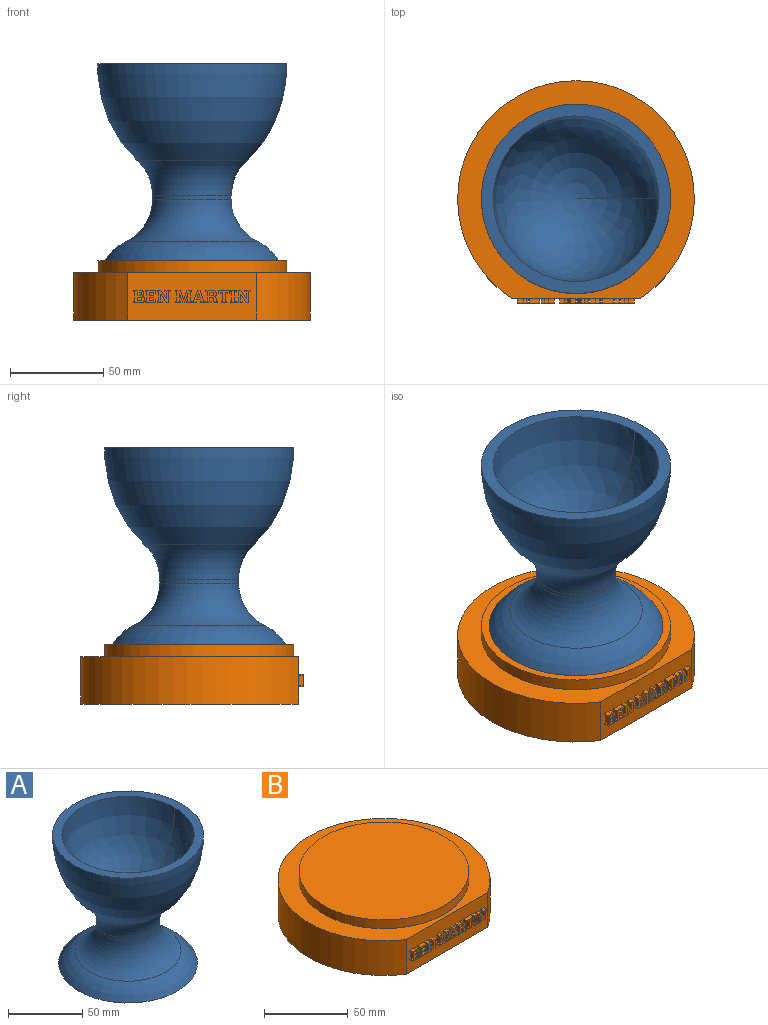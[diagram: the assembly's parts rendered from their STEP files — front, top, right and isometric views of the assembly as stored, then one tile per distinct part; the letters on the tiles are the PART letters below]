
ASSEMBLY  parts=2 mates=1
PART A: 10 faces, bbox 101.6x101.6x105.7 mm
  f0: plane 101.6x101.6mm, normal (0,0,1), area 1900.2mm2, adj f2,f7,f8,f9
  f1: cylinder r=21.22mm len=42.44mm, axis (0,0,-1), area 284.2mm2, adj f5,f6
  f2: revolved ~51.56x21.15mm, area 4.4mm2, adj f0,f6,f8
  f3: plane 93.24x93.24mm, normal (0,0,-1), area 6828.6mm2, adj f4
  f4: torus R=24.62mm, axis (0,0,1), area 3982.6mm2, adj f3,f5
  f5: torus R=46.62mm, axis (0,0,-1), area 4701.5mm2, adj f1,f4
  f6: torus R=46.62mm, axis (0,0,-1), area 3226.2mm2, adj f1,f2,f8
  f7: revolved ~57.15x44.45mm, area 4.1mm2, adj f0,f9
  f8: revolved ~101.6x101.6mm, area 15777.6mm2, adj f0,f2,f6
  f9: revolved ~88.9x88.9mm, area 14832.9mm2, adj f0,f7
PART B: 225 faces, bbox 127x119.4x31.8 mm
  f0: plane 68.91x25.4mm, normal (0,-1,0), area 1517.6mm2, adj f1,f2,f3,f18,f19,f20,f21,f22
  f1: plane 127x116.84mm, normal (0,0,-1), area 12192.9mm2, adj f0,f2
  f2: cylinder r=63.5mm len=127mm, axis (0,0,1), area 8284.1mm2, adj f0,f1,f3
  f3: plane 127x116.84mm, normal (0,0,1), area 4085.6mm2, adj f0,f2,f4
  f4: cylinder r=50.8mm len=101.6mm, axis (0,0,1), area 2026.8mm2, adj f3,f5
  f5: plane 101.6x101.6mm, normal (0,0,1), area 8107.3mm2, adj f4
  f6: plane 2.54x1mm, normal (0,0,1), area 2.5mm2, adj f7,f34,f35,f36
  f7: plane 2.54x1.84mm, normal (1,0,0), area 4.7mm2, adj f6,f8,f35,f36
  f8: plane 2.54x0.95mm, normal (0,0,-1), area 2.4mm2, adj f7,f9,f35,f36
  f9: extruded ~2.54x0.9mm, area 2.4mm2, adj f8,f10,f35,f36
  f10: extruded ~2.54x0.71mm, area 2mm2, adj f9,f11,f35,f36
  f11: extruded ~2.54x0.67mm, area 1.9mm2, adj f10,f34,f35,f36
  f12: plane 2.54x2mm, normal (1,0,0), area 5.1mm2, adj f13,f32,f35,f37
  f13: plane 2.54x1.39mm, normal (0,0,-1), area 3.5mm2, adj f12,f14,f35,f37
  f14: extruded ~2.54x0.78mm, area 2.2mm2, adj f13,f15,f35,f37
  f15: extruded ~2.54x0.78mm, area 2.1mm2, adj f14,f16,f35,f37
  f16: extruded ~2.54x0.71mm, area 2mm2, adj f15,f17,f35,f37
  f17: extruded ~2.54x0.84mm, area 2.3mm2, adj f16,f32,f35,f37
  f18: extruded ~2.54x1.91mm, area 5.1mm2, adj f0,f19,f33,f35
  f19: plane 3.09x2.54mm, normal (0,0,1), area 7.8mm2, adj f0,f18,f20,f35
  f20: plane 2.54x0.84mm, normal (-1,0,0), area 2.1mm2, adj f0,f19,f21,f35
  f21: plane 2.54x0.74mm, normal (-0.19,0,-0.98), area 1.9mm2, adj f0,f20,f22,f35
  f22: plane 4.98x2.54mm, normal (-1,0,0), area 12.7mm2, adj f0,f21,f23,f35
  f23: plane 2.54x0.74mm, normal (-0.19,0,0.98), area 1.9mm2, adj f0,f22,f24,f35
  f24: plane 2.54x0.84mm, normal (-1,0,0), area 2.1mm2, adj f0,f23,f25,f35
  f25: plane 3.42x2.54mm, normal (0,0,-1), area 8.7mm2, adj f0,f24,f26,f35
  f26: extruded ~2.54x1.86mm, area 5mm2, adj f0,f25,f27,f35
  f27: extruded ~2.54x1.51mm, area 4.3mm2, adj f0,f26,f28,f35
  f28: extruded ~2.54x1.02mm, area 2.7mm2, adj f0,f27,f29,f35
  f29: extruded ~2.54x0.94mm, area 2.9mm2, adj f0,f28,f30,f35
  f30: extruded ~2.54x0.74mm, area 2.4mm2, adj f0,f29,f31,f35
  f31: extruded ~2.54x0.86mm, area 2.3mm2, adj f0,f30,f33,f35
  f32: plane 2.54x1.28mm, normal (0,0,1), area 3.3mm2, adj f12,f17,f35,f37
  f33: extruded ~2.54x1.43mm, area 4.2mm2, adj f0,f18,f31,f35
  f34: extruded ~2.54x0.86mm, area 2.3mm2, adj f6,f11,f35,f36
  f35: plane 6.94x5.94mm, normal (0,-1,0), area 25.9mm2, adj f6,f7,f8,f9,f10,f11,f12,f13
  f36: plane 2.16x1.84mm, normal (0,-1,0), area 3.6mm2, adj f6,f7,f8,f9,f10,f11,f34
  f37: plane 2.42x2mm, normal (0,-1,0), area 4.5mm2, adj f12,f13,f14,f15,f16,f17,f32
  f38: plane 2.54x2.35mm, normal (0,0,-1), area 6mm2, adj f0,f39,f57,f58
  f39: plane 2.54x1.07mm, normal (1,0,0), area 2.7mm2, adj f0,f38,f40,f58
  f40: plane 2.54x2.35mm, normal (0,0,1), area 6mm2, adj f0,f39,f41,f58
  f41: plane 2.54x1.75mm, normal (1,0,0), area 4.4mm2, adj f0,f40,f42,f58
  f42: plane 2.54x2.22mm, normal (0,0,-1), area 5.6mm2, adj f0,f41,f43,f58
  f43: plane 2.54x0.83mm, normal (-1,0,-0.08), area 2.1mm2, adj f0,f42,f44,f58
  f44: plane 2.54x1.07mm, normal (0,0,-1), area 2.7mm2, adj f0,f43,f45,f58
  f45: plane 2.54x1.9mm, normal (1,0,0), area 4.8mm2, adj f0,f44,f46,f58
  f46: plane 5.49x2.54mm, normal (0,0,1), area 13.9mm2, adj f0,f45,f47,f58
  f47: plane 2.54x0.84mm, normal (-1,0,0), area 2.1mm2, adj f0,f46,f48,f58
  f48: plane 2.54x0.74mm, normal (-0.19,0,-0.98), area 1.9mm2, adj f0,f47,f49,f58
  f49: plane 4.98x2.54mm, normal (-1,0,0), area 12.7mm2, adj f0,f48,f50,f58
  f50: plane 2.54x0.74mm, normal (-0.19,0,0.98), area 1.9mm2, adj f0,f49,f51,f58
  f51: plane 2.54x0.84mm, normal (-1,0,0), area 2.1mm2, adj f0,f50,f52,f58
  f52: plane 5.49x2.54mm, normal (0,0,-1), area 14mm2, adj f0,f51,f53,f58
  f53: plane 2.54x1.9mm, normal (1,0,0), area 4.8mm2, adj f0,f52,f54,f58
  f54: plane 2.54x1.06mm, normal (0,0,1), area 2.7mm2, adj f0,f53,f55,f58
  f55: plane 2.54x0.83mm, normal (-1,0,0.07), area 2.1mm2, adj f0,f54,f56,f58
  f56: plane 2.54x2.24mm, normal (0,0,1), area 5.7mm2, adj f0,f55,f57,f58
  f57: plane 2.54x1.98mm, normal (1,0,0), area 5mm2, adj f0,f38,f56,f58
  f58: plane 6.94x5.49mm, normal (0,-1,0), area 22.6mm2, adj f38,f39,f40,f41,f42,f43,f44,f45
  f59: plane 2.54x0.84mm, normal (1,0,0), area 2.1mm2, adj f0,f60,f80,f81
  f60: plane 2.88x2.54mm, normal (0,0,1), area 7.3mm2, adj f0,f59,f61,f81
  f61: plane 2.54x0.84mm, normal (-1,0,0), area 2.1mm2, adj f0,f60,f62,f81
  f62: plane 2.54x0.74mm, normal (-0.19,0,-0.98), area 1.9mm2, adj f0,f61,f63,f81
  f63: plane 3.69x2.54mm, normal (-1,0,0), area 9.4mm2, adj f0,f62,f64,f81
  f64: plane 2.54x0.03mm, normal (-0.16,0,0.99), area 0.1mm2, adj f0,f63,f65,f81
  f65: plane 4.67x2.8mm, normal (0.86,0,0.51), area 13.8mm2, adj f0,f64,f66,f81
  f66: plane 2.54x2.13mm, normal (0,0,1), area 5.4mm2, adj f0,f65,f67,f81
  f67: plane 2.54x0.84mm, normal (-1,0,0), area 2.1mm2, adj f0,f66,f68,f81
  f68: plane 2.54x0.74mm, normal (-0.19,0,-0.98), area 1.9mm2, adj f0,f67,f69,f81
  f69: plane 4.98x2.54mm, normal (-1,0,0), area 12.7mm2, adj f0,f68,f70,f81
  f70: plane 2.54x0.74mm, normal (-0.19,0,0.98), area 1.9mm2, adj f0,f69,f71,f81
  f71: plane 2.54x0.84mm, normal (-1,0,0), area 2.1mm2, adj f0,f70,f72,f81
  f72: plane 2.88x2.54mm, normal (0,0,-1), area 7.3mm2, adj f0,f71,f73,f81
  f73: plane 2.54x0.84mm, normal (1,0,0), area 2.1mm2, adj f0,f72,f74,f81
  f74: plane 2.54x0.74mm, normal (0.19,0,0.98), area 1.9mm2, adj f0,f73,f75,f81
  f75: plane 3.69x2.54mm, normal (1,0,0), area 9.4mm2, adj f0,f74,f76,f81
  f76: plane 2.54x0.03mm, normal (0.21,0,-0.98), area 0.1mm2, adj f0,f75,f77,f81
  f77: plane 4.68x2.8mm, normal (-0.86,0,-0.51), area 13.8mm2, adj f0,f76,f78,f81
  f78: plane 2.54x1.39mm, normal (0,0,-1), area 3.5mm2, adj f0,f77,f79,f81
  f79: plane 5.96x2.54mm, normal (1,0,0), area 15.1mm2, adj f0,f78,f80,f81
  f80: plane 2.54x0.74mm, normal (0.19,0,-0.98), area 1.9mm2, adj f0,f59,f79,f81
  f81: plane 7.1x6.94mm, normal (0,-1,0), area 29mm2, adj f59,f60,f61,f62,f63,f64,f65,f66
  f82: plane 2.54x0.03mm, normal (-0.16,0,-0.99), area 0.1mm2, adj f0,f83,f111,f112
  f83: plane 3.07x2.54mm, normal (-1,0,0.04), area 7.8mm2, adj f0,f82,f84,f112
  f84: plane 2.54x1.09mm, normal (-1,0,0), area 2.8mm2, adj f0,f83,f85,f112
  f85: plane 2.54x0.74mm, normal (-0.19,0,0.98), area 1.9mm2, adj f0,f84,f86,f112
  f86: plane 2.54x0.84mm, normal (-1,0,0), area 2.1mm2, adj f0,f85,f87,f112
  f87: plane 2.88x2.54mm, normal (0,0,-1), area 7.3mm2, adj f0,f86,f88,f112
  f88: plane 2.54x0.84mm, normal (1,0,0), area 2.1mm2, adj f0,f87,f89,f112
  f89: plane 2.54x0.74mm, normal (0.19,0,0.98), area 1.9mm2, adj f0,f88,f90,f112
  f90: plane 4.98x2.54mm, normal (1,0,0), area 12.7mm2, adj f0,f89,f91,f112
  f91: plane 2.54x0.74mm, normal (0.19,0,-0.98), area 1.9mm2, adj f0,f90,f92,f112
  f92: plane 2.54x0.84mm, normal (1,0,0), area 2.1mm2, adj f0,f91,f93,f112
  f93: plane 2.57x2.54mm, normal (0,0,1), area 6.5mm2, adj f0,f92,f94,f112
  f94: plane 5.12x2.54mm, normal (-0.94,0,0.33), area 13.8mm2, adj f0,f93,f95,f112
  f95: plane 2.54x0.03mm, normal (0,0,1), area 0.1mm2, adj f0,f94,f96,f112
  f96: plane 5.12x2.54mm, normal (0.95,0,0.33), area 13.8mm2, adj f0,f95,f97,f112
  f97: plane 2.56x2.54mm, normal (0,0,1), area 6.5mm2, adj f0,f96,f98,f112
  f98: plane 2.54x0.84mm, normal (-1,0,0), area 2.1mm2, adj f0,f97,f99,f112
  f99: plane 2.54x0.74mm, normal (-0.19,0,-0.98), area 1.9mm2, adj f0,f98,f100,f112
  f100: plane 4.98x2.54mm, normal (-1,0,0), area 12.7mm2, adj f0,f99,f101,f112
  f101: plane 2.54x0.74mm, normal (-0.19,0,0.98), area 1.9mm2, adj f0,f100,f102,f112
  f102: plane 2.54x0.84mm, normal (-1,0,0), area 2.1mm2, adj f0,f101,f103,f112
  f103: plane 2.88x2.54mm, normal (0,0,-1), area 7.3mm2, adj f0,f102,f104,f112
  f104: plane 2.54x0.84mm, normal (1,0,0), area 2.1mm2, adj f0,f103,f105,f112
  f105: plane 2.54x0.74mm, normal (0.19,0,0.98), area 1.9mm2, adj f0,f104,f106,f112
  f106: plane 2.54x1.09mm, normal (1,0,0), area 2.8mm2, adj f0,f105,f107,f112
  f107: plane 3.05x2.54mm, normal (1,0,0.04), area 7.7mm2, adj f0,f106,f108,f112
  f108: plane 2.54x0.03mm, normal (0.16,0,-0.99), area 0.1mm2, adj f0,f107,f109,f112
  f109: plane 5.12x2.54mm, normal (-0.94,0,-0.34), area 13.8mm2, adj f0,f108,f110,f112
  f110: plane 2.54x0.93mm, normal (0,0,-1), area 2.4mm2, adj f0,f109,f111,f112
  f111: plane 5.14x2.54mm, normal (0.94,0,-0.34), area 13.9mm2, adj f0,f82,f110,f112
  f112: plane 8.7x6.94mm, normal (0,-1,0), area 36.1mm2, adj f82,f83,f84,f85,f86,f87,f88,f89
  f113: plane 2.54x1.59mm, normal (0,0,1), area 4mm2, adj f114,f132,f133,f134
  f114: plane 2.54x2.45mm, normal (0.95,0,-0.3), area 6.5mm2, adj f113,f115,f133,f134
  f115: plane 2.54x0.03mm, normal (0,0,-1), area 0.1mm2, adj f114,f132,f133,f134
  f116: plane 2.54x0.5mm, normal (-0.14,0,0.99), area 1.3mm2, adj f0,f117,f131,f133
  f117: plane 2.54x0.84mm, normal (-1,0,0), area 2.1mm2, adj f0,f116,f118,f133
  f118: plane 2.54x2.37mm, normal (0,0,-1), area 6mm2, adj f0,f117,f119,f133
  f119: plane 2.54x0.84mm, normal (1,0,0), area 2.1mm2, adj f0,f118,f120,f133
  f120: plane 2.54x0.48mm, normal (0.18,0,0.98), area 1.2mm2, adj f0,f119,f121,f133
  f121: plane 2.54x0.95mm, normal (0.95,0,-0.3), area 2.5mm2, adj f0,f120,f122,f133
  f122: plane 2.54x2.25mm, normal (0,0,-1), area 5.7mm2, adj f0,f121,f123,f133
  f123: plane 2.54x0.95mm, normal (-0.95,0,-0.3), area 2.5mm2, adj f0,f122,f124,f133
  f124: plane 2.54x0.48mm, normal (-0.17,0,0.98), area 1.2mm2, adj f0,f123,f125,f133
  f125: plane 2.54x0.84mm, normal (-1,0,0), area 2.1mm2, adj f0,f124,f126,f133
  f126: plane 2.54x2.37mm, normal (0,0,-1), area 6mm2, adj f0,f125,f127,f133
  f127: plane 2.54x0.84mm, normal (1,0,0), area 2.1mm2, adj f0,f126,f128,f133
  f128: plane 2.54x0.5mm, normal (0.14,0,0.99), area 1.3mm2, adj f0,f127,f129,f133
  f129: plane 6.04x2.54mm, normal (0.94,0,0.33), area 16.2mm2, adj f0,f128,f130,f133
  f130: plane 2.54x1.43mm, normal (0,0,1), area 3.6mm2, adj f0,f129,f131,f133
  f131: plane 6.04x2.54mm, normal (-0.94,0,0.33), area 16.2mm2, adj f0,f116,f130,f133
  f132: plane 2.54x2.45mm, normal (-0.95,0,-0.3), area 6.5mm2, adj f113,f115,f133,f134
  f133: plane 6.94x6.63mm, normal (0,-1,0), area 21.1mm2, adj f113,f114,f115,f116,f117,f118,f119,f120
  f134: plane 2.45x1.59mm, normal (0,-1,0), area 2mm2, adj f113,f114,f115,f132
  f135: plane 2.54x0.96mm, normal (0,0,1), area 2.4mm2, adj f136,f169,f170,f171
  f136: plane 2.54x1.99mm, normal (1,0,0), area 5.1mm2, adj f135,f137,f170,f171
  f137: plane 2.54x0.99mm, normal (0,0,-1), area 2.5mm2, adj f136,f138,f170,f171
  f138: extruded ~2.54x0.85mm, area 2.3mm2, adj f137,f139,f170,f171
  f139: extruded ~2.54x0.75mm, area 2.1mm2, adj f138,f140,f170,f171
  f140: extruded ~2.54x0.72mm, area 2mm2, adj f139,f169,f170,f171
  f141: extruded ~2.54x1.86mm, area 5mm2, adj f0,f142,f168,f170
  f142: plane 3.12x2.54mm, normal (0,0,1), area 7.9mm2, adj f0,f141,f143,f170
  f143: plane 2.54x0.84mm, normal (-1,0,0), area 2.1mm2, adj f0,f142,f144,f170
  f144: plane 2.54x0.74mm, normal (-0.19,0,-0.98), area 1.9mm2, adj f0,f143,f145,f170
  f145: plane 4.98x2.54mm, normal (-1,0,0), area 12.7mm2, adj f0,f144,f146,f170
  f146: plane 2.54x0.74mm, normal (-0.19,0,0.98), area 1.9mm2, adj f0,f145,f147,f170
  f147: plane 2.54x0.84mm, normal (-1,0,0), area 2.1mm2, adj f0,f146,f148,f170
  f148: plane 2.88x2.54mm, normal (0,0,-1), area 7.3mm2, adj f0,f147,f149,f170
  f149: plane 2.54x0.84mm, normal (1,0,0), area 2.1mm2, adj f0,f148,f150,f170
  f150: plane 2.54x0.74mm, normal (0.19,0,0.98), area 1.9mm2, adj f0,f149,f151,f170
  f151: plane 2.54x1.83mm, normal (1,0,0), area 4.7mm2, adj f0,f150,f152,f170
  f152: plane 2.54x1.14mm, normal (0,0,-1), area 2.9mm2, adj f0,f151,f153,f170
  f153: extruded ~2.54x0.76mm, area 2.1mm2, adj f0,f152,f154,f170
  f154: extruded ~2.54x0.79mm, area 2.2mm2, adj f0,f153,f155,f170
  f155: plane 2.54x0.4mm, normal (-1,0,0), area 1mm2, adj f0,f154,f156,f170
  f156: extruded ~2.54x0.95mm, area 2.6mm2, adj f0,f155,f157,f170
  f157: extruded ~2.54x0.96mm, area 2.7mm2, adj f0,f156,f158,f170
  f158: plane 2.54x0.72mm, normal (0,0,-1), area 1.8mm2, adj f0,f157,f159,f170
  f159: plane 2.54x0.84mm, normal (1,0,0), area 2.1mm2, adj f0,f158,f160,f170
  f160: plane 2.54x0.17mm, normal (0.14,0,0.99), area 0.4mm2, adj f0,f159,f161,f170
  f161: extruded ~2.54x0.3mm, area 0.9mm2, adj f0,f160,f162,f170
  f162: extruded ~2.54x0.36mm, area 0.9mm2, adj f0,f161,f163,f170
  f163: plane 2.54x0.35mm, normal (1,0,0), area 0.9mm2, adj f0,f162,f164,f170
  f164: extruded ~2.54x1.05mm, area 2.8mm2, adj f0,f163,f165,f170
  f165: extruded ~2.54x0.88mm, area 2.8mm2, adj f0,f164,f166,f170
  f166: extruded ~2.54x0.83mm, area 2.7mm2, adj f0,f165,f167,f170
  f167: extruded ~2.54x0.91mm, area 2.5mm2, adj f0,f166,f168,f170
  f168: extruded ~2.54x1.5mm, area 4.3mm2, adj f0,f141,f167,f170
  f169: extruded ~2.54x0.87mm, area 2.4mm2, adj f135,f140,f170,f171
  f170: plane 6.94x6.26mm, normal (0,-1,0), area 24.9mm2, adj f135,f136,f137,f138,f139,f140,f141,f142
  f171: plane 2.13x1.99mm, normal (0,-1,0), area 3.8mm2, adj f135,f136,f137,f138,f139,f140,f169
  f172: plane 2.54x1.85mm, normal (1,0,0), area 4.7mm2, adj f0,f173,f187,f188
  f173: plane 6.19x2.54mm, normal (0,0,1), area 15.7mm2, adj f0,f172,f174,f188
  f174: plane 2.54x1.85mm, normal (-1,0,0), area 4.7mm2, adj f0,f173,f175,f188
  f175: plane 2.54x1.06mm, normal (0,0,-1), area 2.7mm2, adj f0,f174,f176,f188
  f176: plane 2.54x0.78mm, normal (1,0,-0.07), area 2mm2, adj f0,f175,f177,f188
  f177: plane 2.54x1.27mm, normal (0,0,-1), area 3.2mm2, adj f0,f176,f178,f188
  f178: plane 4.89x2.54mm, normal (-1,0,0), area 12.4mm2, adj f0,f177,f179,f188
  f179: plane 2.54x0.75mm, normal (-0.19,0,0.98), area 1.9mm2, adj f0,f178,f180,f188
  f180: plane 2.54x0.84mm, normal (-1,0,0), area 2.1mm2, adj f0,f179,f181,f188
  f181: plane 2.88x2.54mm, normal (0,0,-1), area 7.3mm2, adj f0,f180,f182,f188
  f182: plane 2.54x0.84mm, normal (1,0,0), area 2.1mm2, adj f0,f181,f183,f188
  f183: plane 2.54x0.75mm, normal (0.19,0,0.98), area 1.9mm2, adj f0,f182,f184,f188
  f184: plane 4.89x2.54mm, normal (1,0,0), area 12.4mm2, adj f0,f183,f185,f188
  f185: plane 2.54x1.28mm, normal (0,0,-1), area 3.2mm2, adj f0,f184,f186,f188
  f186: plane 2.54x0.78mm, normal (-1,0,-0.07), area 2mm2, adj f0,f185,f187,f188
  f187: plane 2.54x1.07mm, normal (0,0,-1), area 2.7mm2, adj f0,f172,f186,f188
  f188: plane 6.94x6.19mm, normal (0,-1,0), area 17.9mm2, adj f172,f173,f174,f175,f176,f177,f178,f179
  f189: plane 2.54x0.84mm, normal (-1,0,0), area 2.1mm2, adj f0,f190,f200,f201
  f190: plane 2.54x0.74mm, normal (-0.19,0,-0.98), area 1.9mm2, adj f0,f189,f191,f201
  f191: plane 4.98x2.54mm, normal (-1,0,0), area 12.7mm2, adj f0,f190,f192,f201
  f192: plane 2.54x0.74mm, normal (-0.19,0,0.98), area 1.9mm2, adj f0,f191,f193,f201
  f193: plane 2.54x0.84mm, normal (-1,0,0), area 2.1mm2, adj f0,f192,f194,f201
  f194: plane 2.88x2.54mm, normal (0,0,-1), area 7.3mm2, adj f0,f193,f195,f201
  f195: plane 2.54x0.84mm, normal (1,0,0), area 2.1mm2, adj f0,f194,f196,f201
  f196: plane 2.54x0.74mm, normal (0.19,0,0.98), area 1.9mm2, adj f0,f195,f197,f201
  f197: plane 4.98x2.54mm, normal (1,0,0), area 12.7mm2, adj f0,f196,f198,f201
  f198: plane 2.54x0.74mm, normal (0.19,0,-0.98), area 1.9mm2, adj f0,f197,f199,f201
  f199: plane 2.54x0.84mm, normal (1,0,0), area 2.1mm2, adj f0,f198,f200,f201
  f200: plane 2.88x2.54mm, normal (0,0,1), area 7.3mm2, adj f0,f189,f199,f201
  f201: plane 6.94x2.88mm, normal (0,-1,0), area 12.3mm2, adj f189,f190,f191,f192,f193,f194,f195,f196
  f202: plane 2.54x0.84mm, normal (1,0,0), area 2.1mm2, adj f0,f203,f223,f224
  f203: plane 2.88x2.54mm, normal (0,0,1), area 7.3mm2, adj f0,f202,f204,f224
  f204: plane 2.54x0.84mm, normal (-1,0,0), area 2.1mm2, adj f0,f203,f205,f224
  f205: plane 2.54x0.74mm, normal (-0.19,0,-0.98), area 1.9mm2, adj f0,f204,f206,f224
  f206: plane 3.69x2.54mm, normal (-1,0,0), area 9.4mm2, adj f0,f205,f207,f224
  f207: plane 2.54x0.03mm, normal (-0.16,0,0.99), area 0.1mm2, adj f0,f206,f208,f224
  f208: plane 4.67x2.8mm, normal (0.86,0,0.51), area 13.8mm2, adj f0,f207,f209,f224
  f209: plane 2.54x2.13mm, normal (0,0,1), area 5.4mm2, adj f0,f208,f210,f224
  f210: plane 2.54x0.84mm, normal (-1,0,0), area 2.1mm2, adj f0,f209,f211,f224
  f211: plane 2.54x0.74mm, normal (-0.19,0,-0.98), area 1.9mm2, adj f0,f210,f212,f224
  f212: plane 4.98x2.54mm, normal (-1,0,0), area 12.7mm2, adj f0,f211,f213,f224
  f213: plane 2.54x0.74mm, normal (-0.19,0,0.98), area 1.9mm2, adj f0,f212,f214,f224
  f214: plane 2.54x0.84mm, normal (-1,0,0), area 2.1mm2, adj f0,f213,f215,f224
  f215: plane 2.88x2.54mm, normal (0,0,-1), area 7.3mm2, adj f0,f214,f216,f224
  f216: plane 2.54x0.84mm, normal (1,0,0), area 2.1mm2, adj f0,f215,f217,f224
  f217: plane 2.54x0.74mm, normal (0.19,0,0.98), area 1.9mm2, adj f0,f216,f218,f224
  f218: plane 3.69x2.54mm, normal (1,0,0), area 9.4mm2, adj f0,f217,f219,f224
  f219: plane 2.54x0.03mm, normal (0.21,0,-0.98), area 0.1mm2, adj f0,f218,f220,f224
  f220: plane 4.68x2.8mm, normal (-0.86,0,-0.51), area 13.8mm2, adj f0,f219,f221,f224
  f221: plane 2.54x1.39mm, normal (0,0,-1), area 3.5mm2, adj f0,f220,f222,f224
  f222: plane 5.96x2.54mm, normal (1,0,0), area 15.1mm2, adj f0,f221,f223,f224
  f223: plane 2.54x0.74mm, normal (0.19,0,-0.98), area 1.9mm2, adj f0,f202,f222,f224
  f224: plane 7.1x6.94mm, normal (0,-1,0), area 29mm2, adj f202,f203,f204,f205,f206,f207,f208,f209
PLACE A t=(152.41,137.19,-59.58)mm
PLACE B t=(172.28,137.19,-98.76)mm
MATE fastened B.f2 <-> A.f1  axis (0,0,1) through (152.41,137.19,-108.97)mm
